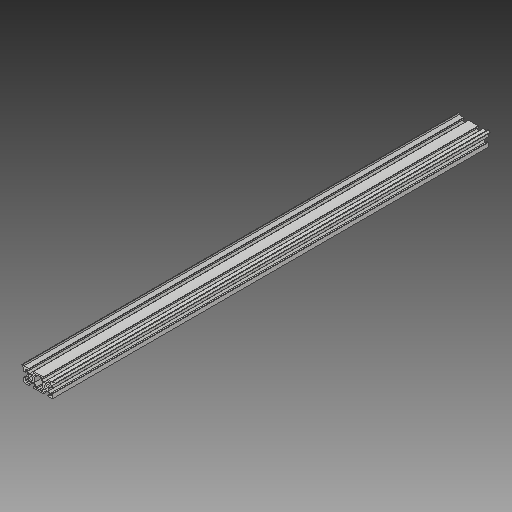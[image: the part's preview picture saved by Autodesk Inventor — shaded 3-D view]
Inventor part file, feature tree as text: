
AUTODESK INVENTOR PART (.ipt)
format: ipt  version: 2018 (Build 220112000, 112)  size: 285,696 bytes
history: native  units: mm
features: other x3, sketch x1
ambient origin geometry x8: Origin, YZ Plane, XZ Plane, XY Plane, X Axis, Y Axis, Z Axis, Center Point
bodies: Solid1 (feature_tree)
feature tree (4):
  other  "Makerslide 600mm.ipt"
  other  "Solid1::Makerslide 600mm.ipt"
  other  "TaggingFeature1"
  sketch  "Sketch1"  dims[d0=10.0mm]
